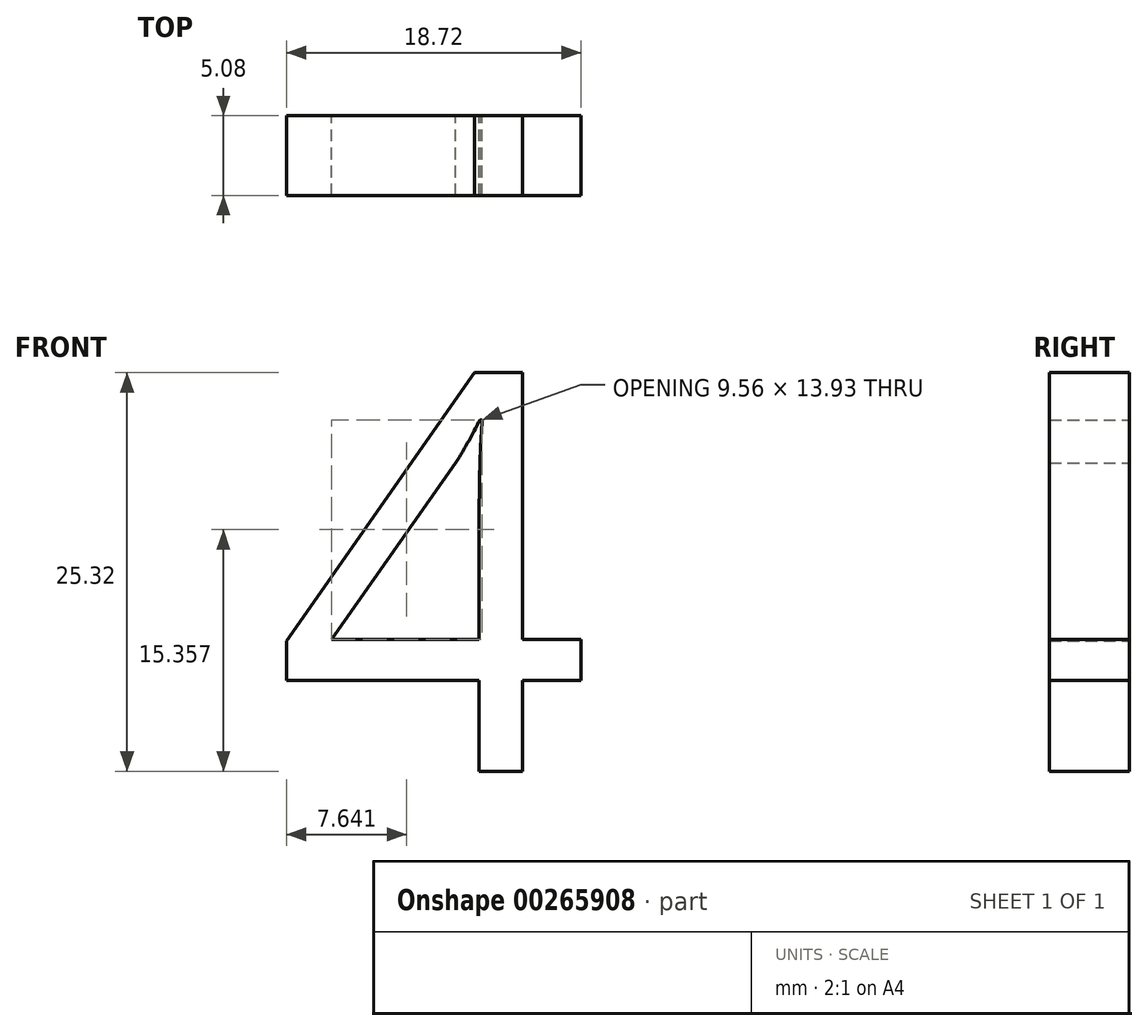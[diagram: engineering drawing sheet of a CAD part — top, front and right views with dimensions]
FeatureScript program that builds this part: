
annotation { "Feature Type Name" : "Feature", "Feature Type Description" : "" }
export const myFeature = defineFeature(function(context is Context, id is Id, definition is map)
    precondition{}
    {
        {
            var Q0;
            Q0=qCreatedBy(makeId("Front.planeOp"),FACE);
            var sketch = newSketch(context, id + "F0", { "sketchPlane" : qUnion([Q0])});
            skText(sketch, "E0", { "text": "4", "fontName": "OpenSans-Regular.ttf"});
            const initialGuessF0  = {"E0": [-0.05278, 0.03098, 1, 0, 0.0254]};
            skSetInitialGuess(sketch, initialGuessF0);
            skSolve(sketch);
        }
        {
            var Q0;
            Q0 = qSketchRegion(id + "F0", true);
            extrude(context, id + "F1", {"entities" : qUnion([Q0]), "depth" : 5.08 * mm});
        }
    });
